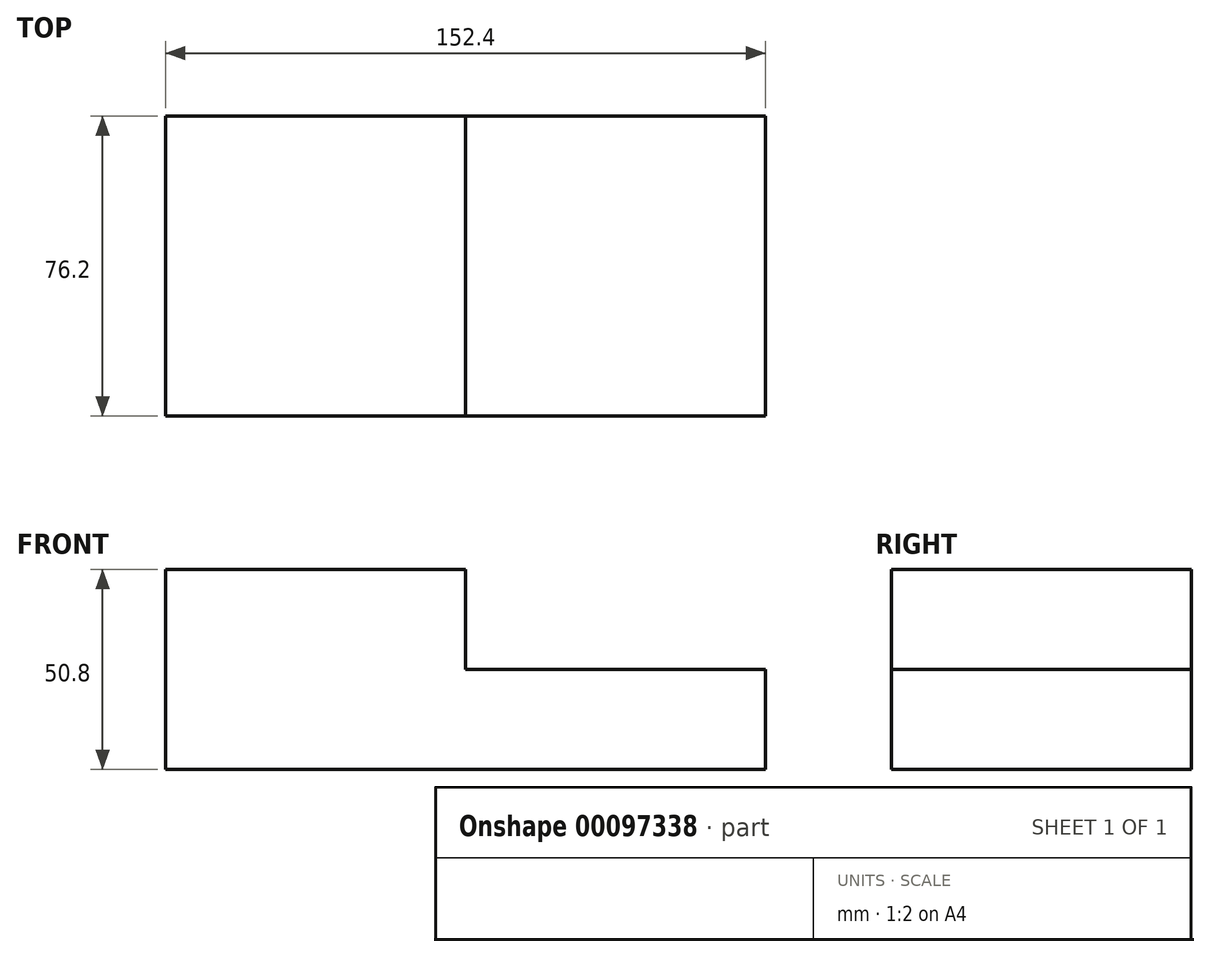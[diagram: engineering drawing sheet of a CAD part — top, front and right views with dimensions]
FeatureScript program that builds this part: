
annotation { "Feature Type Name" : "Feature", "Feature Type Description" : "" }
export const myFeature = defineFeature(function(context is Context, id is Id, definition is map)
    precondition{}
    {
        {
            var Q0;
            Q0=qCreatedBy(makeId("Front.planeOp"),FACE);
            var sketch = newSketch(context, id + "F0", { "sketchPlane" : qUnion([Q0])});
            skLineSegment(sketch, "E0", {"start": v(0, 0) * mm, "end": v(0, 50.8) * mm});
            skLineSegment(sketch, "E1", {"start": v(0, 50.8) * mm, "end": v(76.2, 50.8) * mm});
            skLineSegment(sketch, "E2", {"start": v(76.2, 50.8) * mm, "end": v(76.2, 25.4) * mm});
            skLineSegment(sketch, "E3", {"start": v(76.2, 25.4) * mm, "end": v(152.4, 25.4) * mm});
            skLineSegment(sketch, "E4", {"start": v(152.4, 25.4) * mm, "end": v(152.4, 0) * mm});
            skLineSegment(sketch, "E5", {"start": v(152.4, 0) * mm, "end": v(0, 0) * mm});
            skSolve(sketch);
        }
        {
            var Q0;
            Q0=makeQuery(id+"F0.imprint","IMPRINT",FACE,{"disambiguationData":[TD([[makeQuery(id+"F0.imprint","IMPRINT",EDGE,{"derivedFrom":sQuery(id+"F0.wireOp",EDGE,"E0")}),-1.0]])]});
            extrude(context, id + "F1", {"entities" : qUnion([Q0]), "depth" : 76.2 * mm, "symmetric" : true});
        }
    });
